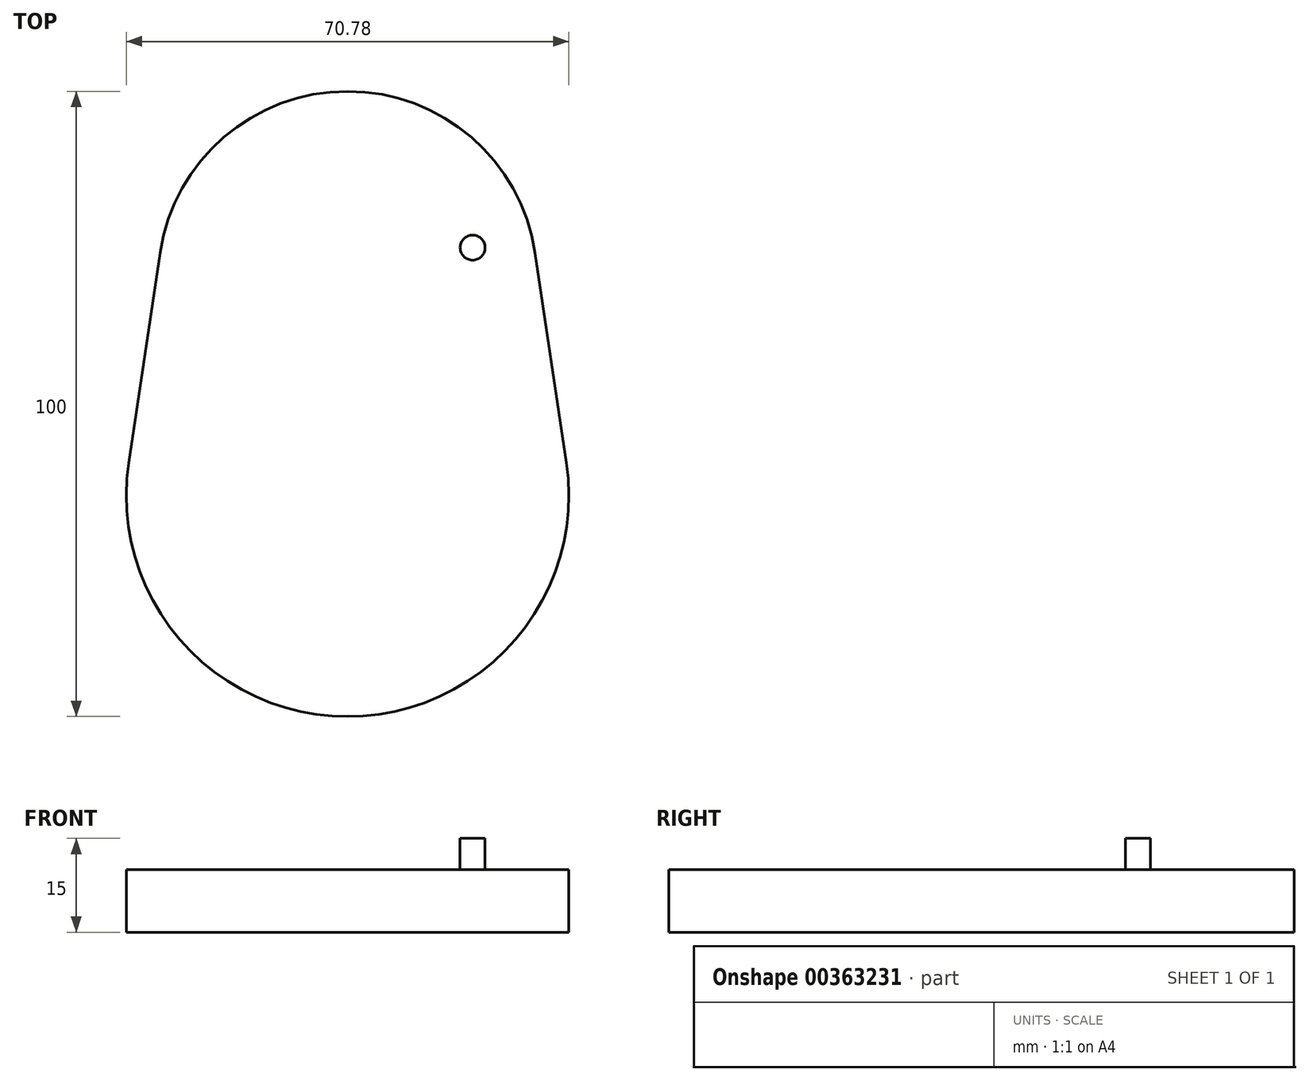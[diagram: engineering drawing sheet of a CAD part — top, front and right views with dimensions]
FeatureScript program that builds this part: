
annotation { "Feature Type Name" : "Feature", "Feature Type Description" : "" }
export const myFeature = defineFeature(function(context is Context, id is Id, definition is map)
    precondition{}
    {
        {
            var Q0;
            Q0=qCreatedBy(makeId("Top.planeOp"),FACE);
            var sketch = newSketch(context, id + "F0", { "sketchPlane" : qUnion([Q0])});
            skLineSegment(sketch, "E0", {"start": v(-30, 45.84) * mm, "end": v(-35, 12.3) * mm});
            skLineSegment(sketch, "E1.MirrorCS", {"start": v(30, 45.84) * mm, "end": v(35, 12.3) * mm});
            skArc(sketch, "E2", {"start": v(-30, 45.84) * mm, "mid": v(0, 71.7) * mm, "end": v(30, 45.84) * mm});
            skArc(sketch, "E3", {"start": v(-35, 12.3) * mm, "mid": v(0, -28.3) * mm, "end": v(35, 12.3) * mm});
            skSolve(sketch);
        }
        {
            var Q0;
            Q0=makeQuery(id+"F0.imprint","IMPRINT",FACE,{"disambiguationData":[TD([[makeQuery(id+"F0.imprint","IMPRINT",EDGE,{"derivedFrom":sQuery(id+"F0.wireOp",EDGE,"E0")}),1.0]])]});
            extrude(context, id + "F1", {"entities" : qUnion([Q0]), "depth" : 15 * mm});
        }
        {
            var Q0;
            Q0=makeQuery(id+"F1.opExtrude","CAP_FACE",FACE,{"disambiguationData":[OSD([sQuery(id+"F0.wireOp",EDGE,"E0"),sQuery(id+"F0.wireOp",EDGE,"E1.MirrorCS"),sQuery(id+"F0.wireOp",EDGE,"E2"),sQuery(id+"F0.wireOp",EDGE,"E3")])],"isStart":false});
            var sketch = newSketch(context, id + "F2", { "sketchPlane" : qUnion([Q0])});
            skLineSegment(sketch, "E4.0.0", {"start": v(35, 12.3) * mm, "end": v(30, 45.84) * mm});
            skArc(sketch, "E4.0.1", {"start": v(30, 45.84) * mm, "mid": v(0, 71.7) * mm, "end": v(-30, 45.84) * mm});
            skLineSegment(sketch, "E4.0.2", {"start": v(-30, 45.84) * mm, "end": v(-35, 12.3) * mm});
            skArc(sketch, "E4.0.3", {"start": v(-35, 12.3) * mm, "mid": v(0, -28.3) * mm, "end": v(35, 12.3) * mm});
            skCircle(sketch, "E5", {"center": v(0, 7.08) * mm, "radius": 15 * mm});
            skSolve(sketch);
        }
        {
            var Q0;
            Q0=makeQuery(id+"F2.imprint","IMPRINT",FACE,{"disambiguationData":[TD([[makeQuery(id+"F2.imprint","IMPRINT",EDGE,{"derivedFrom":sQuery(id+"F2.wireOp",EDGE,"E5")}),1.0]])]});
            extrude(context, id + "F3", {"entities" : qUnion([Q0]), "operationType" : NewBodyOperationType.REMOVE, "oppositeDirection" : true, "depth" : 5 * mm});
        }
        {
            var Q0;
            Q0=makeQuery(id+"F1.opExtrude","CAP_FACE",FACE,{"disambiguationData":[OSD([sQuery(id+"F0.wireOp",EDGE,"E0"),sQuery(id+"F0.wireOp",EDGE,"E1.MirrorCS"),sQuery(id+"F0.wireOp",EDGE,"E2"),sQuery(id+"F0.wireOp",EDGE,"E3")])],"isStart":false});
            var sketch = newSketch(context, id + "F4", { "sketchPlane" : qUnion([Q0])});
            skCircle(sketch, "E6", {"center": v(-20, 46.7) * mm, "radius": 2 * mm});
            skCircle(sketch, "E7.MirrorC", {"center": v(20, 46.7) * mm, "radius": 2 * mm});
            skSolve(sketch);
        }
        {
            var Q0;
            Q0=makeQuery(id+"F4.imprint","IMPRINT",FACE,{"disambiguationData":[TD([[makeQuery(id+"F4.imprint","IMPRINT",EDGE,{"derivedFrom":sQuery(id+"F4.wireOp",EDGE,"E6")}),1.0]])]});
            var Q1;
            Q1=makeQuery(id+"F4.imprint","IMPRINT",FACE,{"disambiguationData":[TD([[makeQuery(id+"F4.imprint","IMPRINT",EDGE,{"derivedFrom":sQuery(id+"F4.wireOp",EDGE,"E7.MirrorC")}),-1.0]])]});
            extrude(context, id + "F5", {"entities" : qUnion([Q0, Q1]), "operationType" : NewBodyOperationType.REMOVE, "oppositeDirection" : true, "depth" : 5 * mm});
        }
    });
